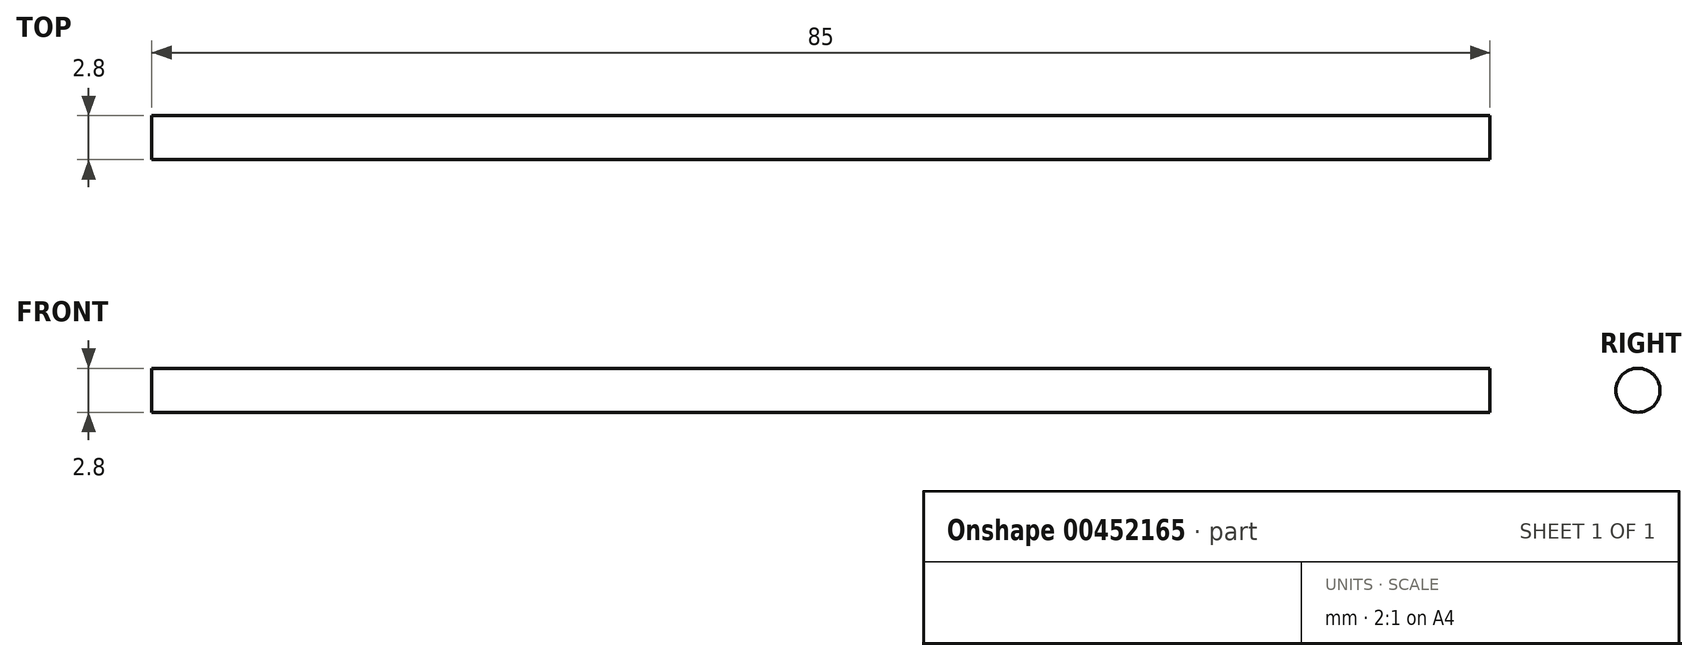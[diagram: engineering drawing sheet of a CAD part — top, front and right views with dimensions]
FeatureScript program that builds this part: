
annotation { "Feature Type Name" : "Feature", "Feature Type Description" : "" }
export const myFeature = defineFeature(function(context is Context, id is Id, definition is map)
    precondition{}
    {
        {
            var Q0;
            Q0=qCreatedBy(makeId("Right.planeOp"),FACE);
            var sketch = newSketch(context, id + "F0", { "sketchPlane" : qUnion([Q0])});
            skCircle(sketch, "E0", {"center": v(0, 0) * mm, "radius": 1.4 * mm});
            skSolve(sketch);
        }
        {
            var Q0;
            Q0 = qSketchRegion(id + "F0", true);
            extrude(context, id + "F1", {"entities" : qUnion([Q0]), "depth" : 85 * mm});
        }
    });
